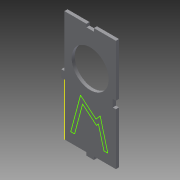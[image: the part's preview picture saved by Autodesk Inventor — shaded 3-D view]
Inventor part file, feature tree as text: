
AUTODESK INVENTOR PART (.ipt)
format: ipt  version: 2015 (Build 190159000, 159)  size: 157,696 bytes
history: native  units: in
note: dims shown in document units (in); Inventor stores cm internally (conversion verified against a paired STEP export)
features: sketch x5, extrude x4
ambient origin geometry x8: Origin, YZ Plane, XZ Plane, XY Plane, X Axis, Y Axis, Z Axis, Center Point
bodies: Solid1 (feature_tree)
feature tree (9):
  extrude  "Extrusion1"  Depth=2.084in
  sketch  "Sketch2"  dims[d2=0.125in d3=0.0in d4=0.15in]
  extrude  "Extrusion2"  Depth=0.125in
  extrude  "Extrusion3"  Depth=0.125in
  sketch  "Sketch3"  dims[d5=0.3in d6=0.125in]
  sketch  "Sketch4"  dims[d7=0.15in d8=0.3in]
  sketch  "Sketch5"  dims[d9=0.125in d13=0.3in d14=0.15in d15=0.125in d16=0.125in d17=0.0in d18=0.125in d19=0.0in d20=0.3in d21=0.15in d22=0.125in d23=1.5in d24=3.0in d25=1.041in d26=0.15in d27=0.15in d29=0.15in d31=75.0deg d32=1.5in d33=0.25in d34=75.0deg d35=0.15in d36=1.15in d38=0.4466in d39=0.2in d40=1.0in d41=0.0in]
  extrude  "Extrusion4"  Depth=0.3in
  sketch  "Sketch1"  dims[d0=4.5in d1=2.084in]
